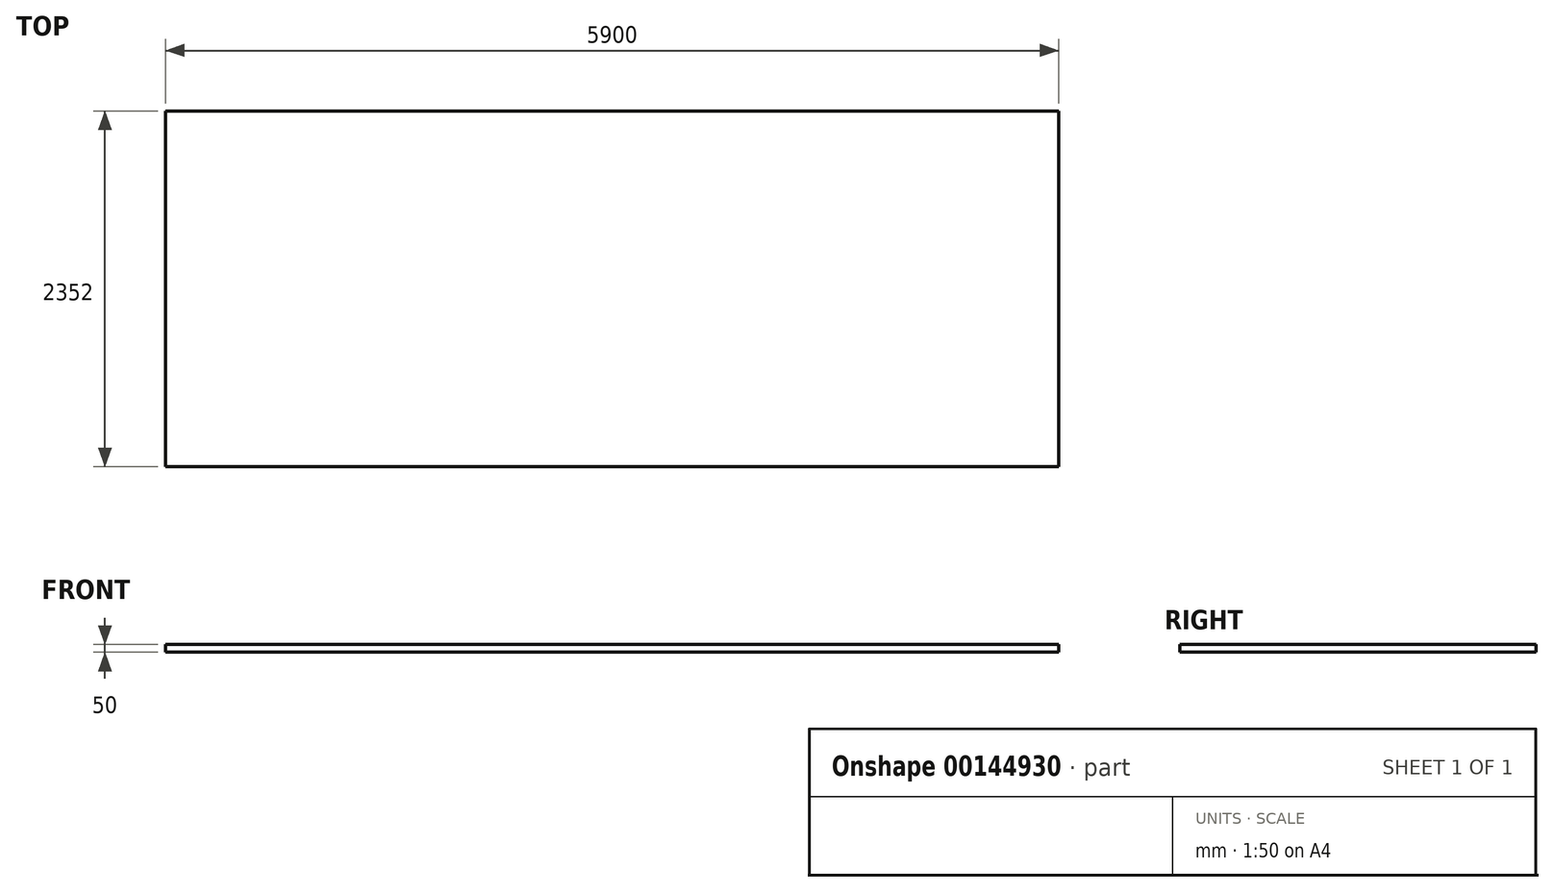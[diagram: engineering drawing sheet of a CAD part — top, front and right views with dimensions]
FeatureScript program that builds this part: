
annotation { "Feature Type Name" : "Feature", "Feature Type Description" : "" }
export const myFeature = defineFeature(function(context is Context, id is Id, definition is map)
    precondition{}
    {
        {
            var Q0;
            Q0=qCreatedBy(makeId("Top.planeOp"),FACE);
            var sketch = newSketch(context, id + "F0", { "sketchPlane" : qUnion([Q0])});
            skLineSegment(sketch, "E0.bottom", {"start": v(2950, -1176) * mm, "end": v(-2950, -1176) * mm});
            skLineSegment(sketch, "E0.top", {"start": v(2950, 1176) * mm, "end": v(-2950, 1176) * mm});
            skLineSegment(sketch, "E0.left", {"start": v(2950, -1176) * mm, "end": v(2950, 1176) * mm});
            skLineSegment(sketch, "E0.right", {"start": v(-2950, -1176) * mm, "end": v(-2950, 1176) * mm});
            skPoint(sketch, "E0.middle", {"position": v(0, 0) * mm});
            skSolve(sketch);
        }
        {
            var Q0;
            Q0=makeQuery(id+"F0.imprint","IMPRINT",FACE,{"disambiguationData":[TD([[makeQuery(id+"F0.imprint","IMPRINT",EDGE,{"derivedFrom":sQuery(id+"F0.wireOp",EDGE,"E0.bottom")}),-1.0]])]});
            extrude(context, id + "F1", {"entities" : qUnion([Q0]), "depth" : 50 * mm});
        }
    });
